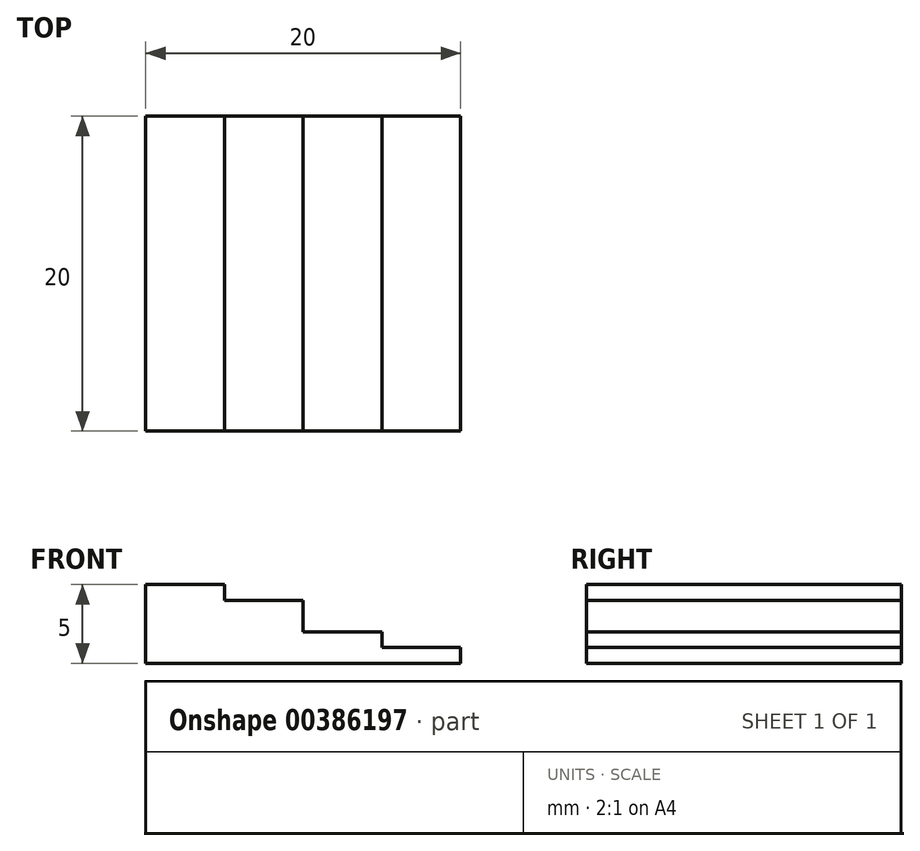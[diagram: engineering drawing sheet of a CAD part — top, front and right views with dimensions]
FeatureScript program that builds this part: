
annotation { "Feature Type Name" : "Feature", "Feature Type Description" : "" }
export const myFeature = defineFeature(function(context is Context, id is Id, definition is map)
    precondition{}
    {
        {
            var Q0;
            Q0=qCreatedBy(makeId("Top.planeOp"),FACE);
            var sketch = newSketch(context, id + "F0", { "sketchPlane" : qUnion([Q0])});
            skLineSegment(sketch, "E0.bottom", {"start": v(0, 0) * mm, "end": v(5, 0) * mm});
            skLineSegment(sketch, "E0.top", {"start": v(0, 20) * mm, "end": v(5, 20) * mm});
            skLineSegment(sketch, "E0.left", {"start": v(0, 0) * mm, "end": v(0, 20) * mm});
            skLineSegment(sketch, "E0.right", {"start": v(5, 0) * mm, "end": v(5, 20) * mm});
            skLineSegment(sketch, "E1.bottom", {"start": v(5, 0) * mm, "end": v(10, 0) * mm});
            skLineSegment(sketch, "E1.top", {"start": v(5, 20) * mm, "end": v(10, 20) * mm});
            skLineSegment(sketch, "E1.right", {"start": v(10, 0) * mm, "end": v(10, 20) * mm});
            skLineSegment(sketch, "E2.bottom", {"start": v(10, 0) * mm, "end": v(15, 0) * mm});
            skLineSegment(sketch, "E2.top", {"start": v(10, 20) * mm, "end": v(15, 20) * mm});
            skLineSegment(sketch, "E2.right", {"start": v(15, 0) * mm, "end": v(15, 20) * mm});
            skLineSegment(sketch, "E3.bottom", {"start": v(15, 0) * mm, "end": v(20, 0) * mm});
            skLineSegment(sketch, "E3.top", {"start": v(15, 20) * mm, "end": v(20, 20) * mm});
            skLineSegment(sketch, "E3.right", {"start": v(20, 0) * mm, "end": v(20, 20) * mm});
            skSolve(sketch);
        }
        {
            var Q0;
            Q0=makeQuery(id+"F0.imprint","IMPRINT",FACE,{"disambiguationData":[TD([[makeQuery(id+"F0.imprint","IMPRINT",EDGE,{"derivedFrom":sQuery(id+"F0.wireOp",EDGE,"E0.bottom")}),1.0]])]});
            extrude(context, id + "F1", {"entities" : qUnion([Q0]), "depth" : 5 * mm, "offsetDistance" : 25 * mm});
        }
        {
            var Q0;
            Q0=makeQuery(id+"F0.imprint","IMPRINT",FACE,{"disambiguationData":[TD([[makeQuery(id+"F0.imprint","IMPRINT",EDGE,{"derivedFrom":sQuery(id+"F0.wireOp",EDGE,"E1.bottom")}),1.0]])]});
            extrude(context, id + "F2", {"entities" : qUnion([Q0]), "operationType" : NewBodyOperationType.ADD, "depth" : 4 * mm, "offsetDistance" : 25 * mm});
        }
        {
            var Q0;
            Q0=makeQuery(id+"F0.imprint","IMPRINT",FACE,{"disambiguationData":[TD([[makeQuery(id+"F0.imprint","IMPRINT",EDGE,{"derivedFrom":sQuery(id+"F0.wireOp",EDGE,"E2.bottom")}),1.0]])]});
            extrude(context, id + "F3", {"entities" : qUnion([Q0]), "operationType" : NewBodyOperationType.ADD, "depth" : 2 * mm, "offsetDistance" : 25 * mm});
        }
        {
            var Q0;
            Q0=makeQuery(id+"F0.imprint","IMPRINT",FACE,{"disambiguationData":[TD([[makeQuery(id+"F0.imprint","IMPRINT",EDGE,{"derivedFrom":sQuery(id+"F0.wireOp",EDGE,"E3.bottom")}),1.0]])]});
            extrude(context, id + "F4", {"entities" : qUnion([Q0]), "operationType" : NewBodyOperationType.ADD, "depth" : 1 * mm, "offsetDistance" : 25 * mm});
        }
    });
